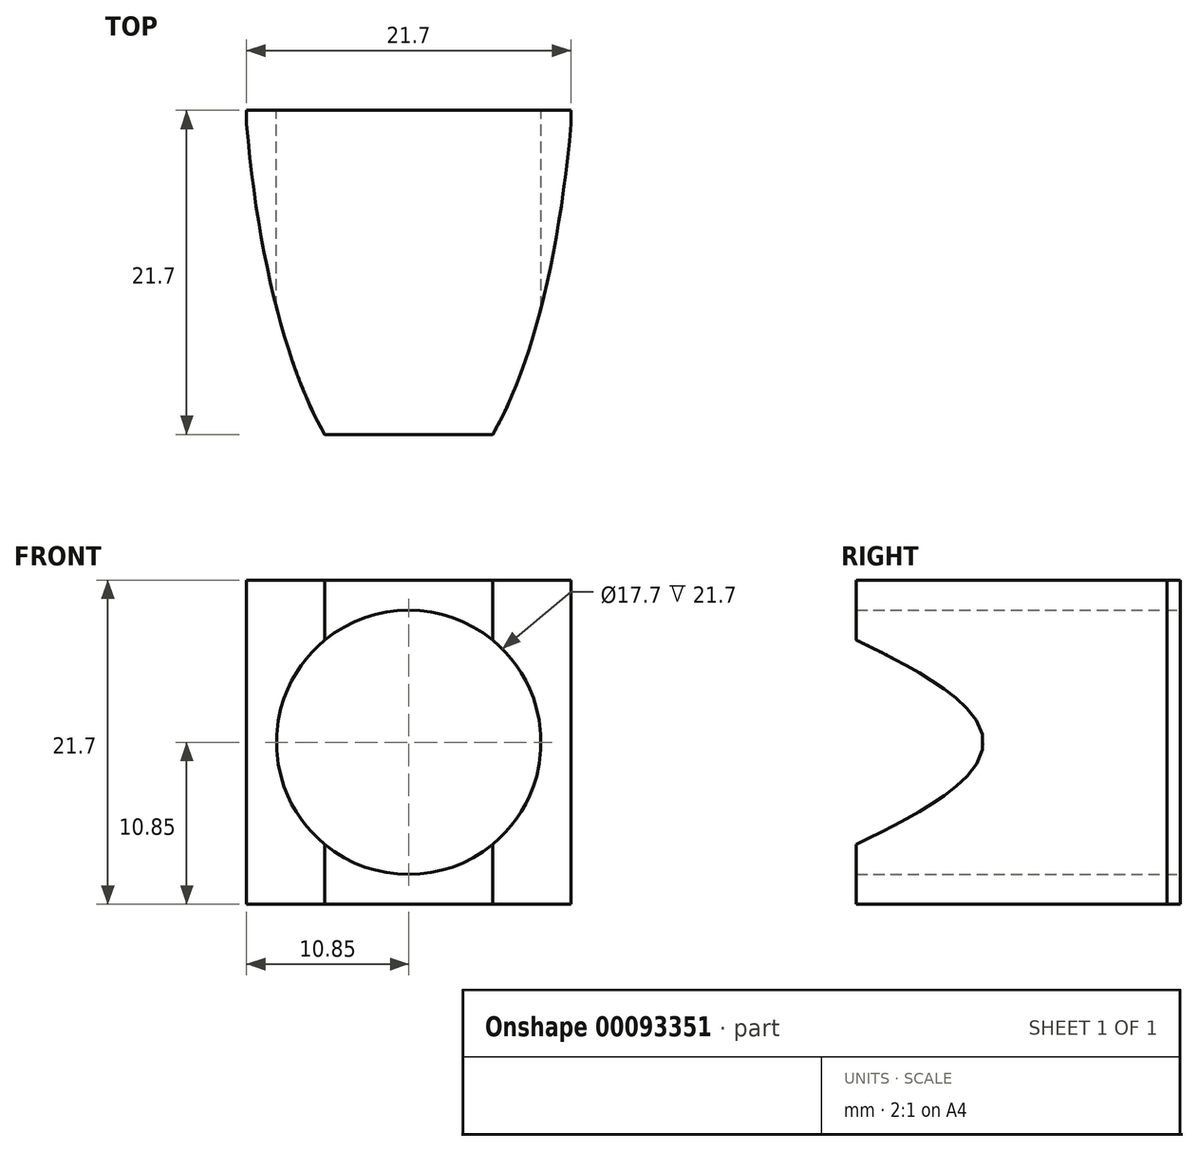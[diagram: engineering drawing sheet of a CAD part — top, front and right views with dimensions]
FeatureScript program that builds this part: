
annotation { "Feature Type Name" : "Feature", "Feature Type Description" : "" }
export const myFeature = defineFeature(function(context is Context, id is Id, definition is map)
    precondition{}
    {
        {
            var Q0;
            Q0=qCreatedBy(makeId("Front.planeOp"),FACE);
            var sketch = newSketch(context, id + "F0", { "sketchPlane" : qUnion([Q0])});
            skLineSegment(sketch, "E0.bottom", {"start": v(8.85, -8.85) * mm, "end": v(-8.85, -8.85) * mm, "construction": true});
            skLineSegment(sketch, "E0.top", {"start": v(8.85, 8.85) * mm, "end": v(-8.85, 8.85) * mm, "construction": true});
            skLineSegment(sketch, "E0.left", {"start": v(8.85, -8.85) * mm, "end": v(8.85, 8.85) * mm, "construction": true});
            skLineSegment(sketch, "E0.right", {"start": v(-8.85, -8.85) * mm, "end": v(-8.85, 8.85) * mm, "construction": true});
            skPoint(sketch, "E0.middle", {"position": v(0, 0) * mm});
            skCircle(sketch, "E1", {"center": v(0, 0) * mm, "radius": 8.85 * mm});
            skLineSegment(sketch, "E2.0", {"start": v(10.85, 10.85) * mm, "end": v(-10.85, 10.85) * mm});
            skLineSegment(sketch, "E2.1", {"start": v(10.85, -10.85) * mm, "end": v(10.85, 10.85) * mm});
            skLineSegment(sketch, "E2.2", {"start": v(10.85, -10.85) * mm, "end": v(-10.85, -10.85) * mm});
            skLineSegment(sketch, "E2.3", {"start": v(-10.85, -10.85) * mm, "end": v(-10.85, 10.85) * mm});
            skSolve(sketch);
        }
        {
            var Q0;
            Q0=makeQuery(id+"F0.imprint","IMPRINT",FACE,{"disambiguationData":[TD([[makeQuery(id+"F0.imprint","IMPRINT",EDGE,{"derivedFrom":sQuery(id+"F0.wireOp",EDGE,"E1")}),-1.0]])]});
            extrude(context, id + "F1", {"entities" : qUnion([Q0]), "depth" : (21.7 / 2) * mm, "hasSecondDirection" : true, "secondDirectionOppositeDirection" : true, "secondDirectionDepth" : 10.85 * mm});
        }
        {
            var Q0;
            Q0=makeQuery(id+"F1.opExtrude","SWEPT_FACE",FACE,{"disambiguationData":[OSD([sQuery(id+"F0.wireOp",EDGE,"E2.0")])]});
            var sketch = newSketch(context, id + "F2", { "sketchPlane" : qUnion([Q0])});
            skLineSegment(sketch, "E3", {"start": v(8.72, 12.78) * mm, "end": v(17.92, 12.78) * mm});
            skLineSegment(sketch, "E4", {"start": v(17.92, 12.78) * mm, "end": v(17.92, -13.9) * mm});
            skLineSegment(sketch, "E5", {"start": v(17.92, -13.9) * mm, "end": v(3.36, -13.9) * mm});
            skLineSegment(sketch, "E6.MirrorCS", {"start": v(-8.72, 12.78) * mm, "end": v(-17.92, 12.78) * mm});
            skLineSegment(sketch, "E7.MirrorCS", {"start": v(-17.92, 12.78) * mm, "end": v(-17.92, -13.9) * mm});
            skLineSegment(sketch, "E8.MirrorCS", {"start": v(-17.92, -13.9) * mm, "end": v(-3.36, -13.9) * mm});
            skEllipse(sketch, "E9", {"center": v(0, 18.35) * mm, "majorRadius": 33.76 * mm, "minorRadius": 11.2 * mm, "majorAxis": v(0, -1)});
            skSolve(sketch);
        }
        {
            var Q0;
            {var subQ0=sQuery(id+"F2.wireOp",EDGE,"E3");Q0=makeQuery(id+"F2.imprint","IMPRINT",FACE,{"disambiguationData":[TD([[makeQuery(id+"F2.imprint","IMPRINT",EDGE,{"derivedFrom":subQ0}),-1.0]])]});}
            var Q1;
            {var subQ0=sQuery(id+"F2.wireOp",EDGE,"E6.MirrorCS");Q1=makeQuery(id+"F2.imprint","IMPRINT",FACE,{"disambiguationData":[TD([[makeQuery(id+"F2.imprint","IMPRINT",EDGE,{"derivedFrom":subQ0}),1.0]])]});}
            var Q2;
            {var subQ1=sQuery(id+"F0.wireOp",EDGE,"E2.0");var subQ6=makeQuery(id+"F1.opExtrude","SWEPT_EDGE",EDGE,{"disambiguationData":[OSD([subQ1,sQuery(id+"F0.wireOp",EDGE,"E2.1")])]});Q2=makeQuery(id+"F2.imprint","IMPRINT",FACE,{"disambiguationData":[TD([[makeQuery(id+"F2.imprint","IMPRINT",EDGE,{"derivedFrom":subQ6}),1.0]])]});}
            var Q3;
            {var subQ1=sQuery(id+"F0.wireOp",EDGE,"E2.0");var subQ6=makeQuery(id+"F1.opExtrude","SWEPT_EDGE",EDGE,{"disambiguationData":[OSD([subQ1,sQuery(id+"F0.wireOp",EDGE,"E2.3")])]});Q3=makeQuery(id+"F2.imprint","IMPRINT",FACE,{"disambiguationData":[TD([[makeQuery(id+"F2.imprint","IMPRINT",EDGE,{"derivedFrom":subQ6}),-1.0]])]});}
            extrude(context, id + "F3", {"entities" : qUnion([Q0, Q1, Q2, Q3]), "operationType" : NewBodyOperationType.REMOVE, "oppositeDirection" : true, "depth" : 25 * mm});
        }
    });
